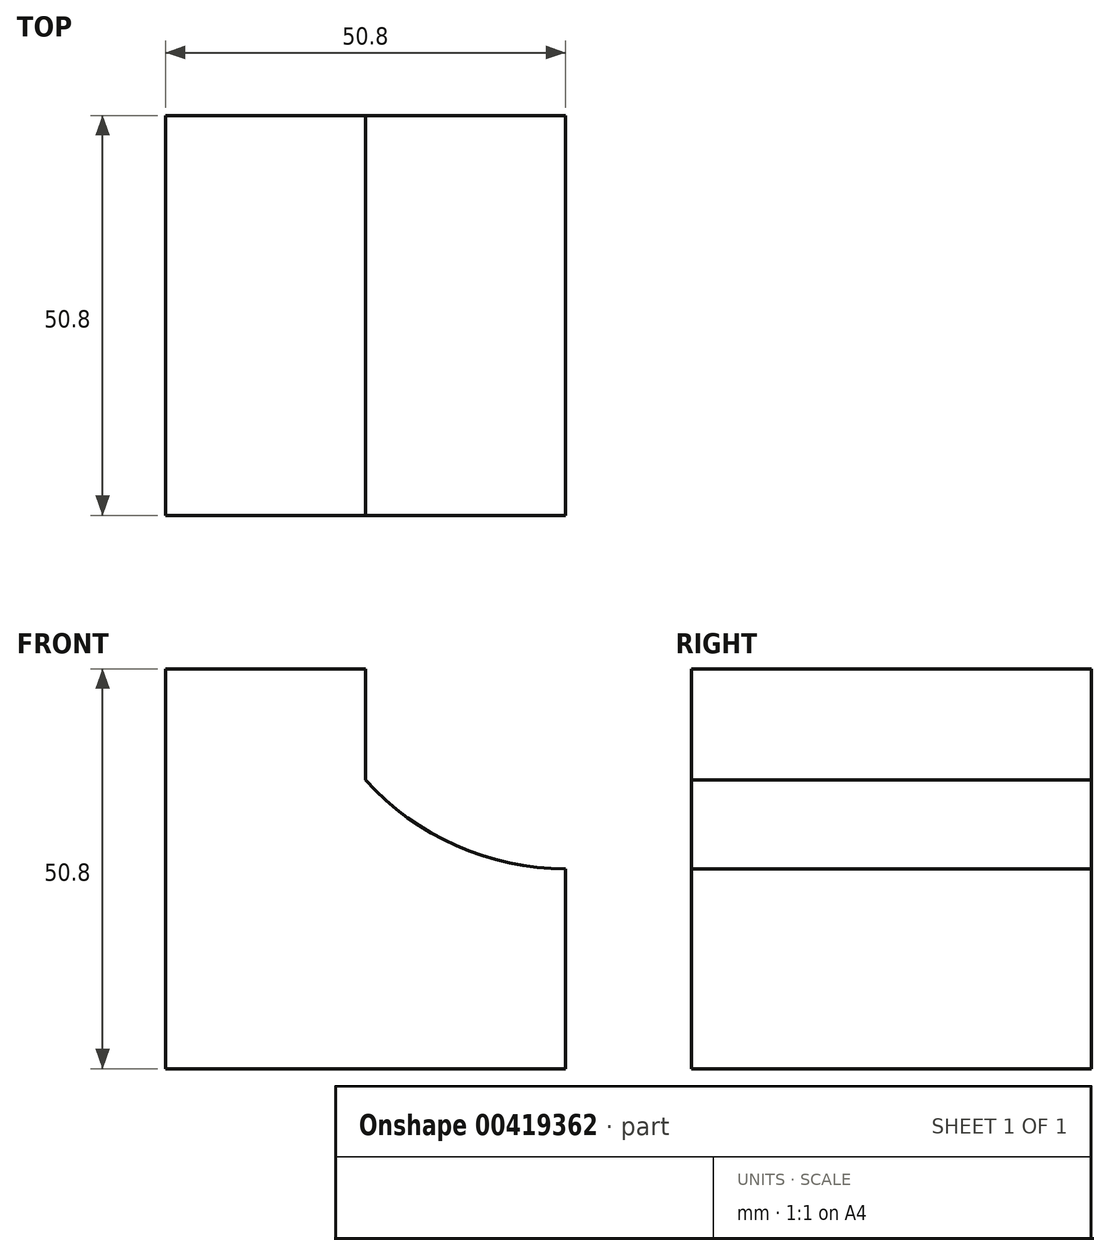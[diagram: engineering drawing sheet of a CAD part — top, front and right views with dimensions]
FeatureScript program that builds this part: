
annotation { "Feature Type Name" : "Feature", "Feature Type Description" : "" }
export const myFeature = defineFeature(function(context is Context, id is Id, definition is map)
    precondition{}
    {
        {
            var Q0;
            Q0=qCreatedBy(makeId("Front.planeOp"),FACE);
            var sketch = newSketch(context, id + "F0", { "sketchPlane" : qUnion([Q0])});
            skLineSegment(sketch, "E0", {"start": v(20.63, 0) * mm, "end": v(-30.17, 0) * mm});
            skLineSegment(sketch, "E1", {"start": v(-30.17, 0) * mm, "end": v(-30.17, 50.8) * mm});
            skLineSegment(sketch, "E2", {"start": v(-30.17, 50.8) * mm, "end": v(-4.77, 50.8) * mm});
            skLineSegment(sketch, "E3", {"start": v(-4.77, 50.8) * mm, "end": v(-4.77, 25.4) * mm});
            skLineSegment(sketch, "E4", {"start": v(-4.77, 25.4) * mm, "end": v(20.62, 25.4) * mm});
            skLineSegment(sketch, "E5", {"start": v(20.62, 25.4) * mm, "end": v(20.63, -1.53) * mm});
            skArc(sketch, "E6", {"start": v(-4.77, 36.66) * mm, "mid": v(6.73, 28.34) * mm, "end": v(20.62, 25.4) * mm});
            skSolve(sketch);
        }
        {
            var Q0;
            Q0 = qSketchRegion(id + "F0", true);
            extrude(context, id + "F1", {"entities" : qUnion([Q0]), "depth" : 50.8 * mm});
        }
    });
